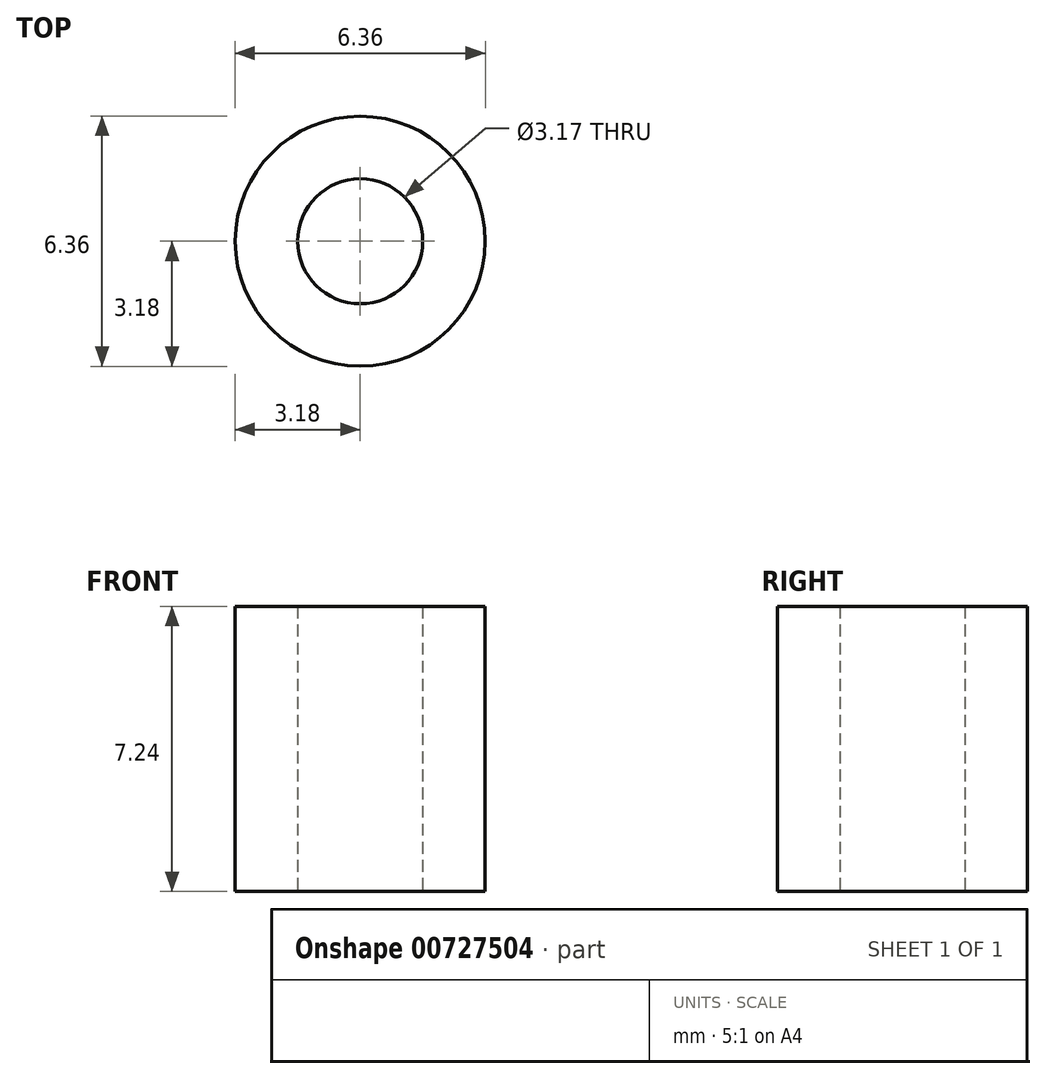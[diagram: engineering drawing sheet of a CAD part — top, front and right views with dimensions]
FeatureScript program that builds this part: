
annotation { "Feature Type Name" : "Feature", "Feature Type Description" : "" }
export const myFeature = defineFeature(function(context is Context, id is Id, definition is map)
    precondition{}
    {
        {
            var Q0;
            Q0=qCreatedBy(makeId("Top.planeOp"),FACE);
            var sketch = newSketch(context, id + "F0", { "sketchPlane" : qUnion([Q0])});
            skCircle(sketch, "E0", {"center": v(0, 0) * mm, "radius": 1.59 * mm});
            skCircle(sketch, "E1", {"center": v(0, 0) * mm, "radius": 3.18 * mm});
            skSolve(sketch);
        }
        {
            var Q0;
            Q0=makeQuery(id+"F0.imprint","IMPRINT",FACE,{"disambiguationData":[TD([[makeQuery(id+"F0.imprint","IMPRINT",EDGE,{"derivedFrom":sQuery(id+"F0.wireOp",EDGE,"E0")}),-1.0]])]});
            extrude(context, id + "F1", {"entities" : qUnion([Q0]), "depth" : 7.24 * mm, "offsetDistance" : 25.4 * mm});
        }
    });
